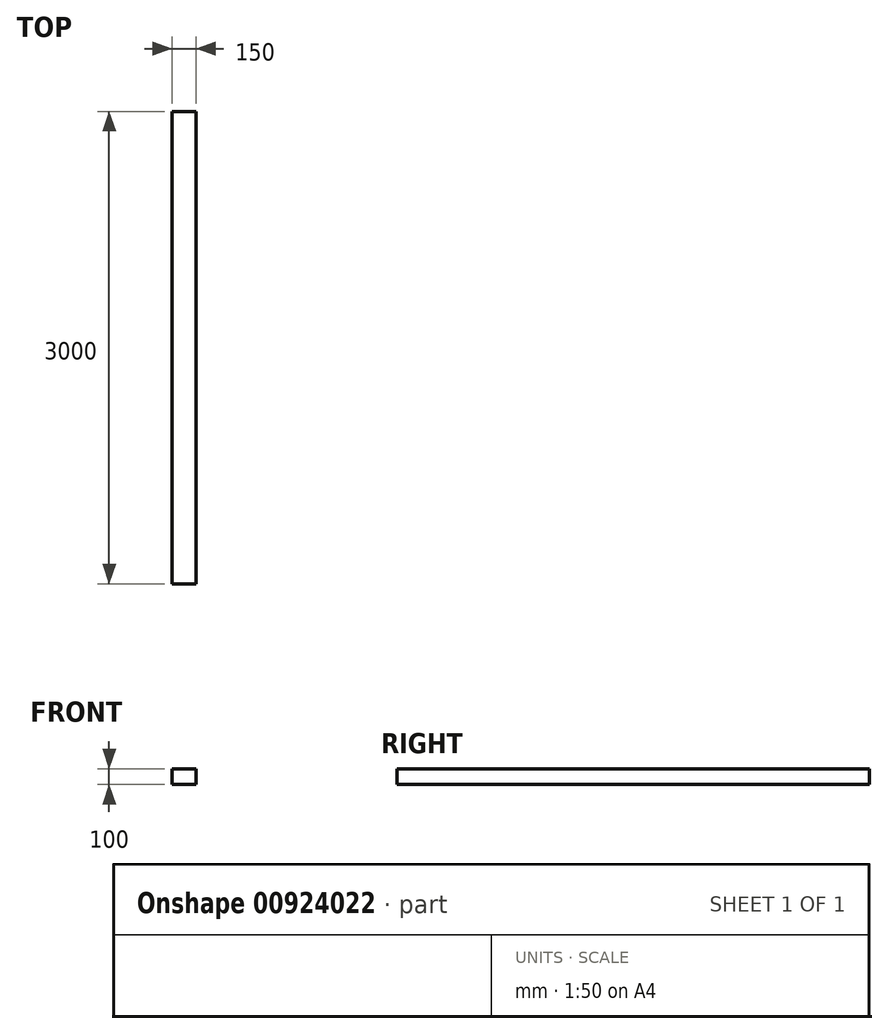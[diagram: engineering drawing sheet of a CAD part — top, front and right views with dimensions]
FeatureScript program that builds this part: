
annotation { "Feature Type Name" : "Feature", "Feature Type Description" : "" }
export const myFeature = defineFeature(function(context is Context, id is Id, definition is map)
    precondition{}
    {
        {
            var Q0;
            Q0=qCreatedBy(makeId("Front.planeOp"),FACE);
            var sketch = newSketch(context, id + "F0", { "sketchPlane" : qUnion([Q0])});
            skLineSegment(sketch, "E0.bottom", {"start": v(0, 0) * mm, "end": v(150, 0) * mm});
            skLineSegment(sketch, "E0.top", {"start": v(0, 100) * mm, "end": v(150, 100) * mm});
            skLineSegment(sketch, "E0.left", {"start": v(0, 0) * mm, "end": v(0, 100) * mm});
            skLineSegment(sketch, "E0.right", {"start": v(150, 0) * mm, "end": v(150, 100) * mm});
            skSolve(sketch);
        }
        {
            var Q0;
            Q0=qSketchRegion(id+"F0",true);
            extrude(context, id + "F1", {"entities" : qUnion([Q0]), "depth" : 3000 * mm, "offsetDistance" : 25 * mm});
        }
    });
